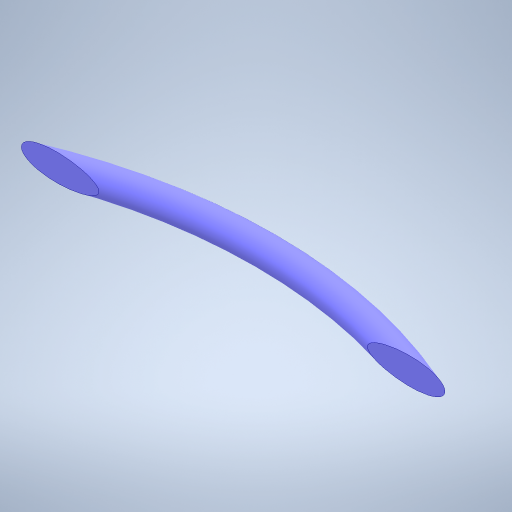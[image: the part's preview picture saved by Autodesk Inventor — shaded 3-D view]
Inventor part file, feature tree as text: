
AUTODESK INVENTOR PART (.ipt)
format: ipt  version: 2024 (Build 280153000, 153)  size: 267,264 bytes
history: native  units: in
note: dims shown in document units (in); Inventor stores cm internally (conversion verified against a paired STEP export)
features: sketch x2, revolve x1, extrude x1
ambient origin geometry x8: Origin, YZ Plane, XZ Plane, XY Plane, X Axis, Y Axis, Z Axis, Center Point
bodies: Solid1 (feature_tree)
feature tree (4):
  revolve  "Revolution1"  [1 undecoded]
  extrude  "Extrusion1"  Depth=11.8425in
  sketch  "Sketch1"  dims[d0=0.75in d1=14.0in]
  sketch  "Sketch2"  dims[d2=90.0deg d3=11.8425in d4=1.0in d5=0.0in]
note: 1 required parameter value undecoded (feature->parameter linkage not recoverable at this tier; creation-order binding heuristic only, values carry confidence <= 0.55)
